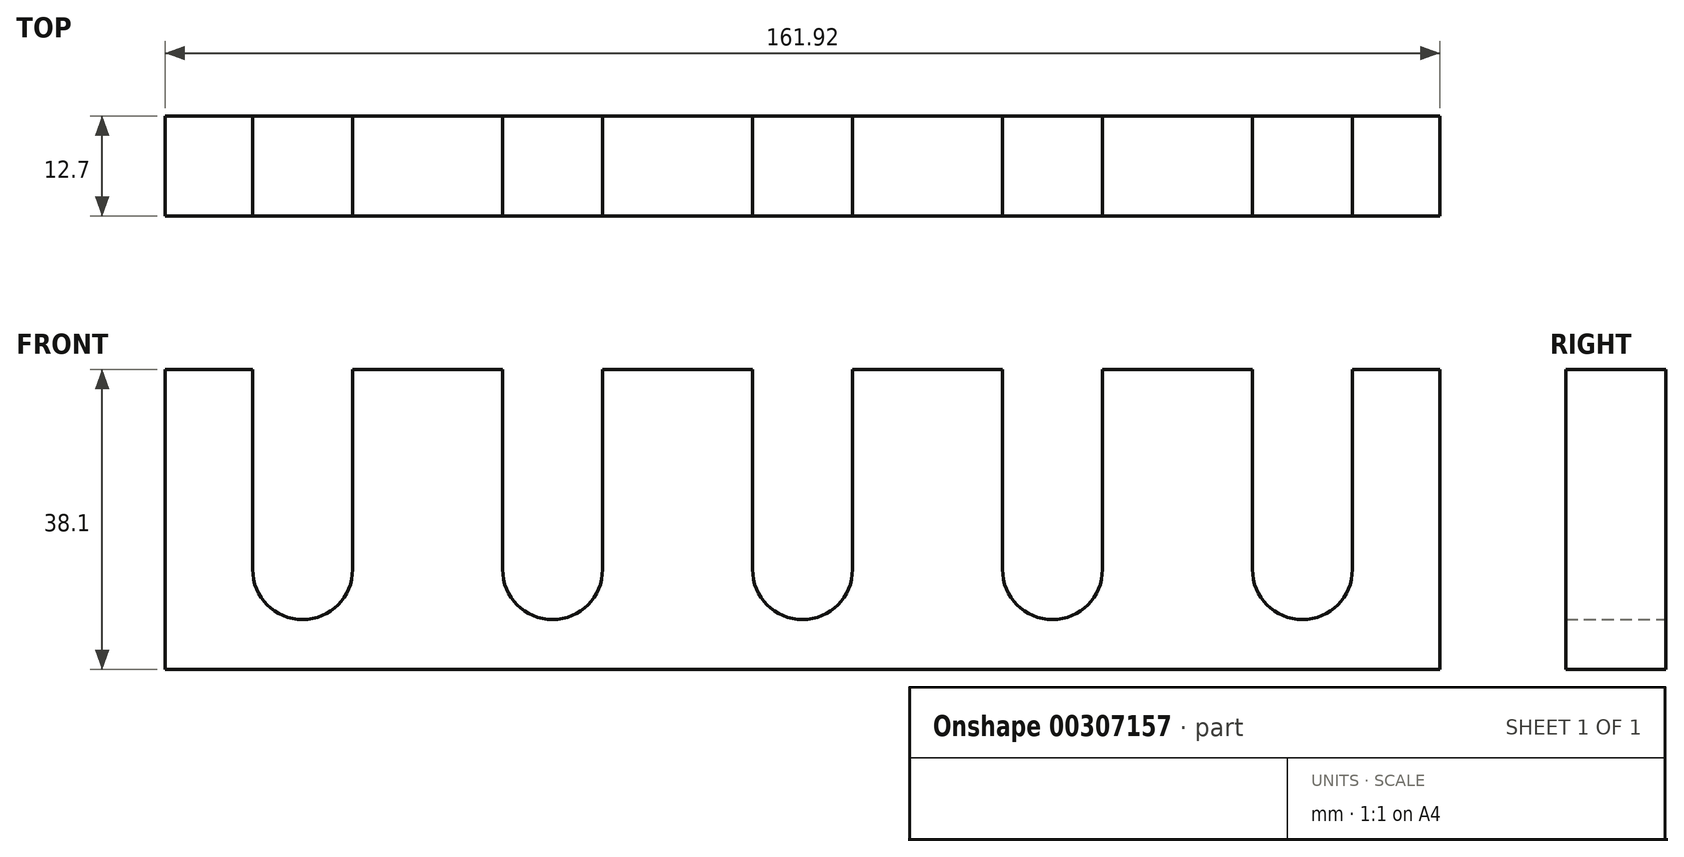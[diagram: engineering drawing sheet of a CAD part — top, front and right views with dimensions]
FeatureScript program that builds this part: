
annotation { "Feature Type Name" : "Feature", "Feature Type Description" : "" }
export const myFeature = defineFeature(function(context is Context, id is Id, definition is map)
    precondition{}
    {
        {
            var Q0;
            Q0=qCreatedBy(makeId("Front.planeOp"),FACE);
            var sketch = newSketch(context, id + "F0", { "sketchPlane" : qUnion([Q0])});
            skLineSegment(sketch, "E0.bottom", {"start": v(80.96, -19.05) * mm, "end": v(-80.96, -19.05) * mm});
            skLineSegment(sketch, "E0.top", {"start": v(80.96, 19.05) * mm, "end": v(-80.96, 19.05) * mm});
            skLineSegment(sketch, "E0.left", {"start": v(80.96, -19.05) * mm, "end": v(80.96, 19.05) * mm});
            skLineSegment(sketch, "E0.right", {"start": v(-80.96, -19.05) * mm, "end": v(-80.96, 19.05) * mm});
            skPoint(sketch, "E0.middle", {"position": v(0, 0) * mm});
            skCircle(sketch, "E1", {"center": v(-63.5, -6.35) * mm, "radius": 6.35 * mm});
            skPoint(sketch, "E2", {"position": v(-69.85, -6.35) * mm});
            skPoint(sketch, "E3", {"position": v(-57.15, -6.35) * mm});
            skLineSegment(sketch, "E4.bottom", {"start": v(-69.85, 19.05) * mm, "end": v(-57.15, 19.05) * mm});
            skLineSegment(sketch, "E4.top", {"start": v(-69.85, -6.35) * mm, "end": v(-57.15, -6.35) * mm});
            skLineSegment(sketch, "E4.left", {"start": v(-69.85, 19.05) * mm, "end": v(-69.85, -6.35) * mm});
            skLineSegment(sketch, "E4.right", {"start": v(-57.15, 19.05) * mm, "end": v(-57.15, -6.35) * mm});
            skPoint(sketch, "E5", {"position": v(-31.75, -6.35) * mm});
            skPoint(sketch, "E6", {"position": v(0, -6.35) * mm});
            skPoint(sketch, "E7", {"position": v(31.75, -6.35) * mm});
            skPoint(sketch, "E8", {"position": v(63.5, -6.35) * mm});
            skCircle(sketch, "E9", {"center": v(-31.75, -6.35) * mm, "radius": 6.35 * mm});
            skCircle(sketch, "E10", {"center": v(0, -6.35) * mm, "radius": 6.35 * mm});
            skCircle(sketch, "E11", {"center": v(31.75, -6.35) * mm, "radius": 6.35 * mm});
            skCircle(sketch, "E12", {"center": v(63.5, -6.35) * mm, "radius": 6.35 * mm});
            skPoint(sketch, "E13", {"position": v(-38.1, -6.35) * mm});
            skPoint(sketch, "E14", {"position": v(-25.4, -6.35) * mm});
            skPoint(sketch, "E15", {"position": v(-6.35, -6.35) * mm});
            skPoint(sketch, "E16", {"position": v(6.35, -6.35) * mm});
            skPoint(sketch, "E17", {"position": v(25.4, -6.35) * mm});
            skPoint(sketch, "E18", {"position": v(38.1, -6.35) * mm});
            skPoint(sketch, "E19", {"position": v(57.15, -6.35) * mm});
            skPoint(sketch, "E20", {"position": v(69.85, -6.35) * mm});
            skLineSegment(sketch, "E21.bottom", {"start": v(-38.1, 19.05) * mm, "end": v(-25.4, 19.05) * mm});
            skLineSegment(sketch, "E21.top", {"start": v(-38.1, -6.35) * mm, "end": v(-25.4, -6.35) * mm});
            skLineSegment(sketch, "E21.left", {"start": v(-38.1, 19.05) * mm, "end": v(-38.1, -6.35) * mm});
            skLineSegment(sketch, "E21.right", {"start": v(-25.4, 19.05) * mm, "end": v(-25.4, -6.35) * mm});
            skLineSegment(sketch, "E22.bottom", {"start": v(-6.35, 19.05) * mm, "end": v(6.35, 19.05) * mm});
            skLineSegment(sketch, "E22.top", {"start": v(-6.35, -6.35) * mm, "end": v(6.35, -6.35) * mm});
            skLineSegment(sketch, "E22.left", {"start": v(-6.35, 19.05) * mm, "end": v(-6.35, -6.35) * mm});
            skLineSegment(sketch, "E22.right", {"start": v(6.35, 19.05) * mm, "end": v(6.35, -6.35) * mm});
            skLineSegment(sketch, "E23.bottom", {"start": v(25.4, 19.05) * mm, "end": v(38.1, 19.05) * mm});
            skLineSegment(sketch, "E23.top", {"start": v(25.4, -6.35) * mm, "end": v(38.1, -6.35) * mm});
            skLineSegment(sketch, "E23.left", {"start": v(25.4, 19.05) * mm, "end": v(25.4, -6.35) * mm});
            skLineSegment(sketch, "E23.right", {"start": v(38.1, 19.05) * mm, "end": v(38.1, -6.35) * mm});
            skLineSegment(sketch, "E24.bottom", {"start": v(57.15, 19.05) * mm, "end": v(69.85, 19.05) * mm});
            skLineSegment(sketch, "E24.top", {"start": v(57.15, -6.35) * mm, "end": v(69.85, -6.35) * mm});
            skLineSegment(sketch, "E24.left", {"start": v(57.15, 19.05) * mm, "end": v(57.15, -6.35) * mm});
            skLineSegment(sketch, "E24.right", {"start": v(69.85, 19.05) * mm, "end": v(69.85, -6.35) * mm});
            skSolve(sketch);
        }
        {
            var Q0;
            Q0=makeQuery(id+"F0.imprint","IMPRINT",FACE,{"disambiguationData":[TD([[makeQuery(id+"F0.imprint","IMPRINT",EDGE,{"derivedFrom":sQuery(id+"F0.wireOp",EDGE,"E0.bottom")}),-1.0]])]});
            extrude(context, id + "F1", {"entities" : qUnion([Q0]), "depth" : 12.7 * mm});
        }
    });
